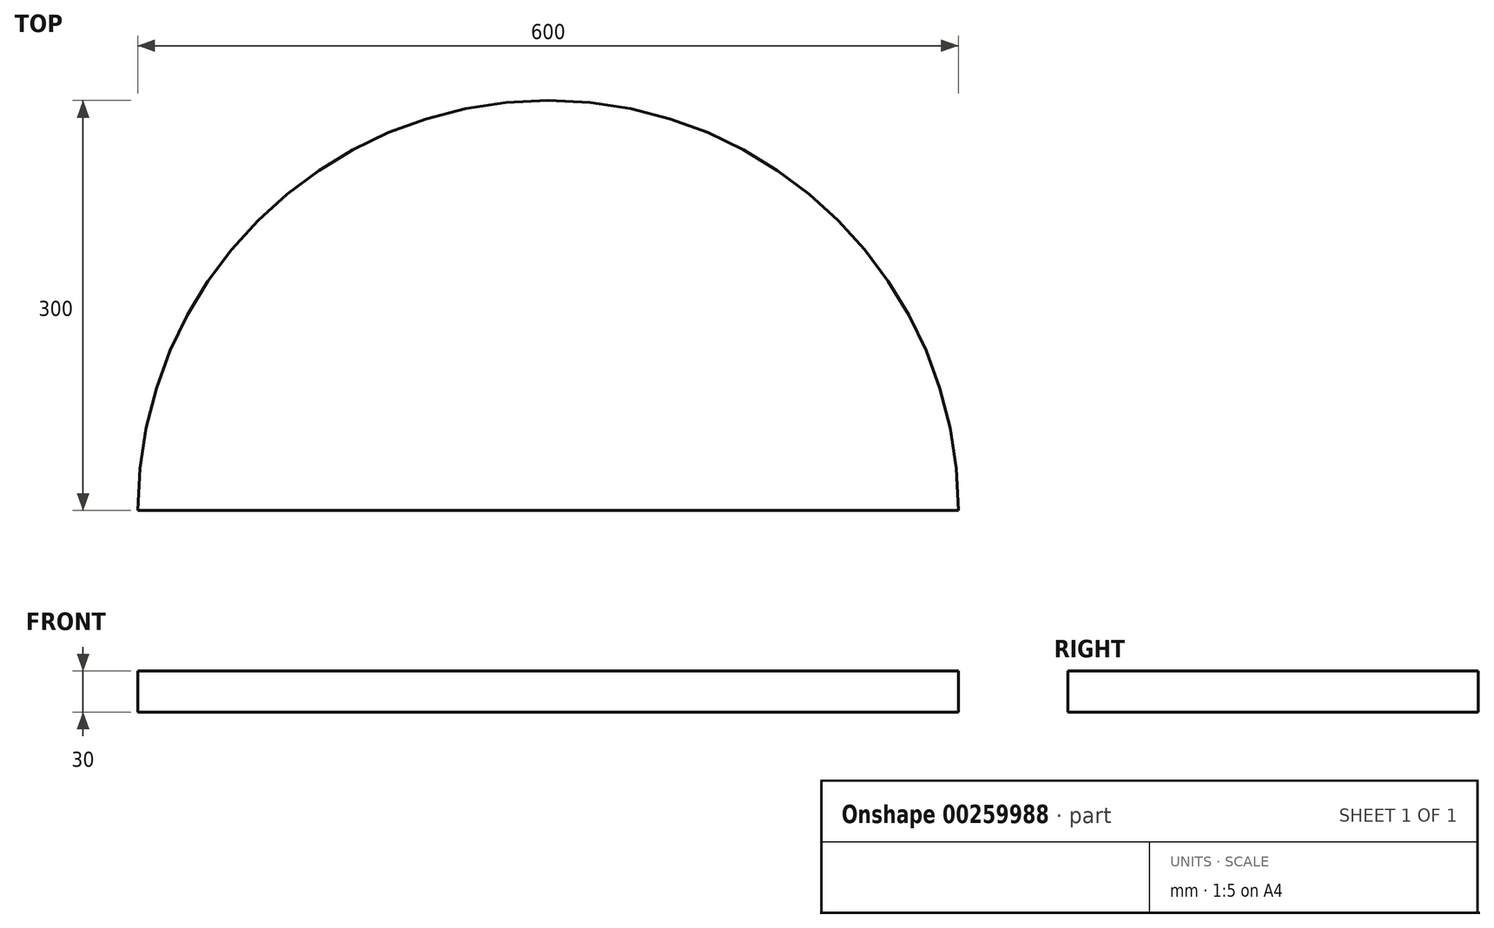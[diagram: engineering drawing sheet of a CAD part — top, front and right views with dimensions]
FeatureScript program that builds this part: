
annotation { "Feature Type Name" : "Feature", "Feature Type Description" : "" }
export const myFeature = defineFeature(function(context is Context, id is Id, definition is map)
    precondition{}
    {
        {
            var Q0;
            Q0=qCreatedBy(makeId("Top.planeOp"),FACE);
            var sketch = newSketch(context, id + "F0", { "sketchPlane" : qUnion([Q0])});
            skLineSegment(sketch, "E0.top", {"start": v(-314.38, -177.34) * mm, "end": v(285.62, -177.34) * mm});
            skArc(sketch, "E1", {"start": v(285.62, -177.34) * mm, "mid": v(-14.38, 122.66) * mm, "end": v(-314.38, -177.34) * mm});
            skSolve(sketch);
        }
        {
            var Q0;
            Q0=makeQuery(id+"F0.imprint","IMPRINT",FACE,{"disambiguationData":[TD([[makeQuery(id+"F0.imprint","IMPRINT",EDGE,{"derivedFrom":sQuery(id+"F0.wireOp",EDGE,"E0.top")}),1.0]])]});
            extrude(context, id + "F1", {"entities" : qUnion([Q0]), "depth" : 30 * mm});
        }
    });
